# Revit family: Haworth_BeHold_Accessory_HAT-Shelf
name_source: partatom
category: Furniture Systems
revit_build: Autodesk Revit 2018 (Build: 20170223_1515(x64)
units: mm (PartAtom-declared; Revit-internal decimal feet)

## family parameters
Always vertical = Yes
Cut with Voids When Loaded = No
OmniClass Number = 23.40.70.14.64.21
OmniClass Title = Systems Furniture
Part Type = Normal
Room Calculation Point = No
Round Connector Dimension = Use Diameter
Shared = No
Work Plane-Based = No

## types (2) — shared parameters
Actual Depth = 6"
Actual Height = 1/2"
Assembly Code = E2020200
Custom Size = No
Description = Haworth - Be_Hold - Accessory - HAT Shelf
Manufacturer = Haworth
Max. Depth = 6"
Max. Width = 36"
Min. Depth = 6"
Min. Width = 30"
Model = Haworth Be_Hold
Revision Number = 1
Shelf Offset = 51/64"
Size = Verify Final Dim. w/ Haworth
Standard Widths = 30, 36 in.
Sustainability Info = https://www.haworth.com
Trim Finish = Haworth _ Paint _ Sky Blue
Warranty = http://www.haworth.com

## per-type parameters (varying)
| type | Actual Width | URL | URL - Product | Width |
| 30w | 30" | http://www.haworth.com | http://www.haworth.com | 30" |
| 36w | 36" | www.haworth.com |  | 36" |

## geometry (parser evidence)
native form markers: Sweep x2
no freeform markers — native parametric forms only
